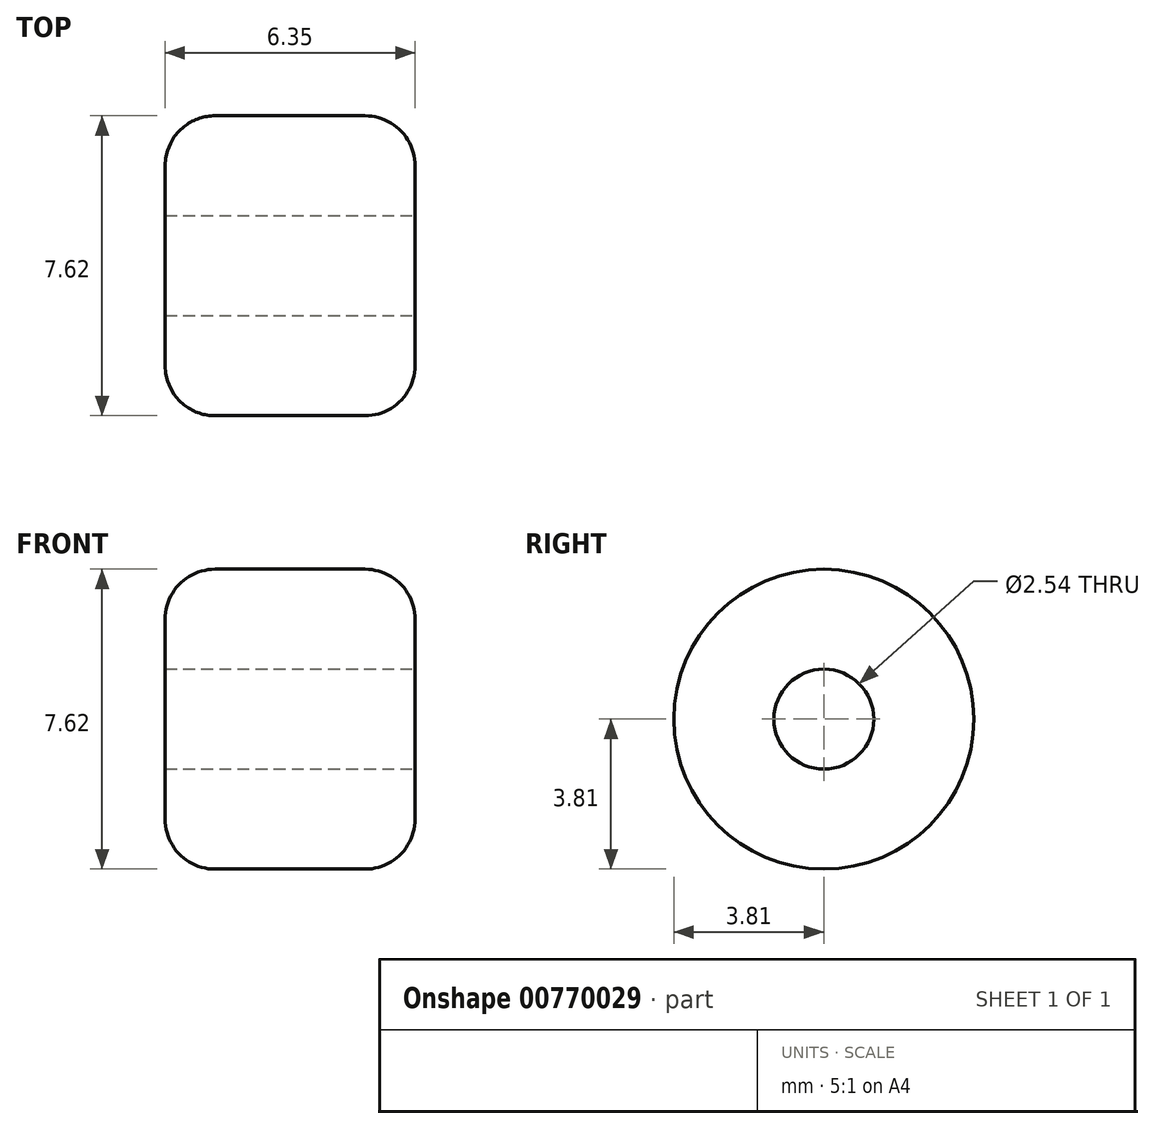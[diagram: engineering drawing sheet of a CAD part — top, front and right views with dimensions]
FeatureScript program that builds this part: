
annotation { "Feature Type Name" : "Feature", "Feature Type Description" : "" }
export const myFeature = defineFeature(function(context is Context, id is Id, definition is map)
    precondition{}
    {
        {
            var Q0;
            Q0=qCreatedBy(makeId("Right.planeOp"),FACE);
            var sketch = newSketch(context, id + "F0", { "sketchPlane" : qUnion([Q0])});
            skCircle(sketch, "E0", {"center": v(0, 0) * mm, "radius": 3.81 * mm});
            skSolve(sketch);
        }
        {
            var Q0;
            Q0 = qSketchRegion(id + "F0", true);
            extrude(context, id + "F1", {"entities" : qUnion([Q0]), "depth" : 6.35 * mm, "offsetDistance" : 25.4 * mm});
        }
        {
            var Q0;
            Q0=makeQuery(id+"F1.opExtrude","CAP_EDGE",EDGE,{"disambiguationData":[OSD([sQuery(id+"F0.wireOp",EDGE,"E0")])],"isStart":false});
            var Q1;
            Q1=makeQuery(id+"F1.opExtrude","CAP_EDGE",EDGE,{"disambiguationData":[OSD([sQuery(id+"F0.wireOp",EDGE,"E0")])],"isStart":true});
            fillet(context, id + "F2", {"entities" : qUnion([Q0, Q1]), "radius" : 1.27 * mm, "tangentPropagation" : true, "allowEdgeOverflow" : false});
        }
        {
            var Q0;
            Q0=makeQuery(id+"F1.opExtrude","CAP_FACE",FACE,{"disambiguationData":[OSD([sQuery(id+"F0.wireOp",EDGE,"E0")])],"isStart":false});
            var sketch = newSketch(context, id + "F3", { "sketchPlane" : qUnion([Q0])});
            skCircle(sketch, "E1", {"center": v(0, 0) * mm, "radius": 1.27 * mm});
            skSolve(sketch);
        }
        {
            var Q0;
            Q0 = qSketchRegion(id + "F3", true);
            extrude(context, id + "F4", {"entities" : qUnion([Q0]), "operationType" : NewBodyOperationType.REMOVE, "oppositeDirection" : true, "depth" : 25.4 * mm, "offsetDistance" : 25.4 * mm});
        }
    });
